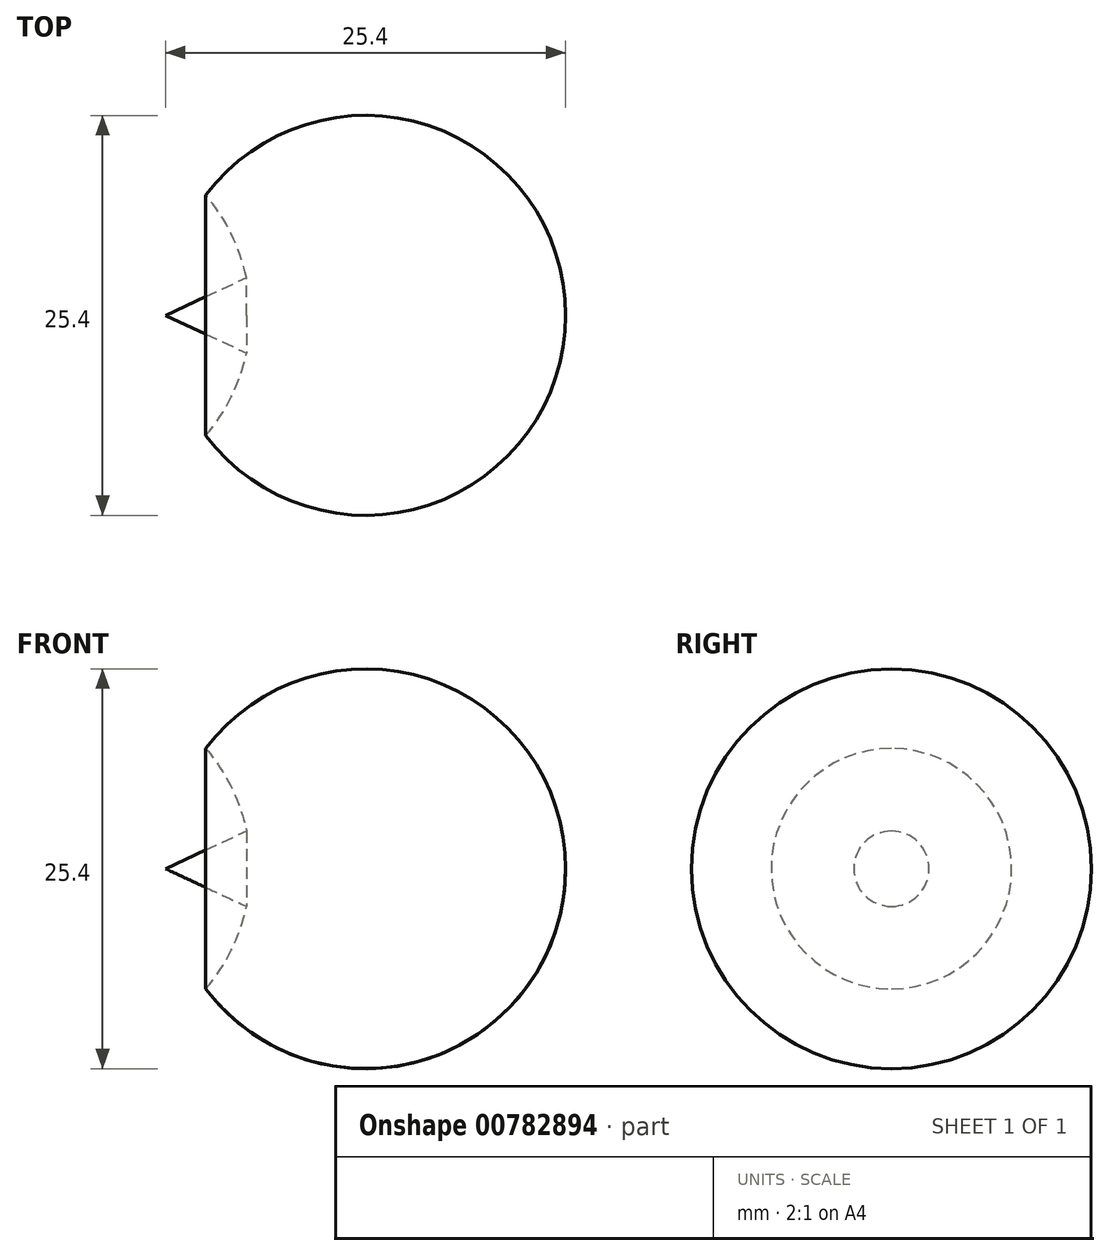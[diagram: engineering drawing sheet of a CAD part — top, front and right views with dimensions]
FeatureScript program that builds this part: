
annotation { "Feature Type Name" : "Feature", "Feature Type Description" : "" }
export const myFeature = defineFeature(function(context is Context, id is Id, definition is map)
    precondition{}
    {
        {
            var Q0;
            Q0=qCreatedBy(makeId("Front.planeOp"),FACE);
            var sketch = newSketch(context, id + "F0", { "sketchPlane" : qUnion([Q0])});
            skLineSegment(sketch, "E0", {"start": v(12.7, 0) * mm, "end": v(-7.32, 0) * mm});
            skArc(sketch, "E1", {"start": v(12.7, 0) * mm, "mid": v(4.03, 12.05) * mm, "end": v(-10.15, 7.64) * mm});
            skArc(sketch, "E2", {"start": v(-7.32, 0) * mm, "mid": v(-8.05, 4.07) * mm, "end": v(-10.15, 7.64) * mm});
            skSolve(sketch);
        }
        {
            var Q0;
            Q0=makeQuery(id+"F0.imprint","IMPRINT",FACE,{"disambiguationData":[TD([[makeQuery(id+"F0.imprint","IMPRINT",EDGE,{"derivedFrom":sQuery(id+"F0.wireOp",EDGE,"E0")}),-1.0]])]});
            var Q1;
            Q1=sQuery(id+"F0.wireOp",EDGE,"E0");
            revolve(context, id + "F1", {"surfaceOperationType" : NewSurfaceOperationType.NEW, "entities" : qUnion([Q0]), "axis" : qUnion([Q1]), "revolveType" : RevolveType.FULL});
        }
        {
            var Q0;
            Q0=qCreatedBy(makeId("Front.planeOp"),FACE);
            var sketch = newSketch(context, id + "F2", { "sketchPlane" : qUnion([Q0])});
            skLineSegment(sketch, "E3", {"start": v(-4.65, 0) * mm, "end": v(-12.7, 0) * mm});
            skLineSegment(sketch, "E4", {"start": v(-12.7, 0) * mm, "end": v(-4.92, 3.63) * mm});
            skLineSegment(sketch, "E5", {"start": v(-4.92, 3.63) * mm, "end": v(-4.65, 0) * mm});
            skSolve(sketch);
        }
        {
            var Q0;
            Q0=makeQuery(id+"F2.imprint","IMPRINT",FACE,{"disambiguationData":[TD([[makeQuery(id+"F2.imprint","IMPRINT",EDGE,{"derivedFrom":sQuery(id+"F2.wireOp",EDGE,"E3")}),-1.0]])]});
            var Q1;
            Q1=sQuery(id+"F2.wireOp",EDGE,"E3");
            revolve(context, id + "F3", {"operationType" : NewBodyOperationType.ADD, "surfaceOperationType" : NewSurfaceOperationType.NEW, "entities" : qUnion([Q0]), "axis" : qUnion([Q1]), "revolveType" : RevolveType.FULL});
        }
    });
